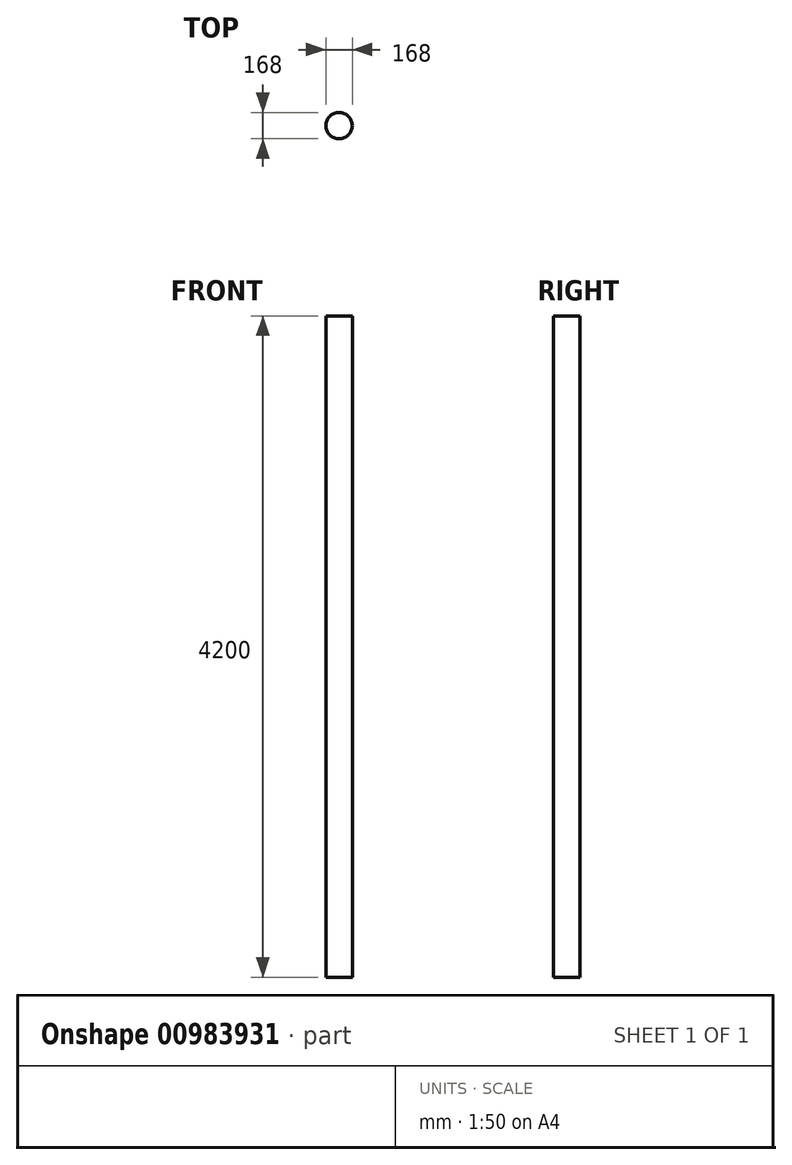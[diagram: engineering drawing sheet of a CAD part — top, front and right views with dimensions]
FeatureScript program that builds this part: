
annotation { "Feature Type Name" : "Feature", "Feature Type Description" : "" }
export const myFeature = defineFeature(function(context is Context, id is Id, definition is map)
    precondition{}
    {
        {
            var Q0;
            Q0=qCreatedBy(makeId("Top.planeOp"),FACE);
            var sketch = newSketch(context, id + "F0", { "sketchPlane" : qUnion([Q0])});
            skCircle(sketch, "E0", {"center": v(0, 0) * mm, "radius": 84 * mm});
            skSolve(sketch);
        }
        {
            var Q0;
            Q0=makeQuery(id+"F0.imprint","IMPRINT",FACE,{"disambiguationData":[TD([[makeQuery(id+"F0.imprint","IMPRINT",EDGE,{"derivedFrom":sQuery(id+"F0.wireOp",EDGE,"E0")}),1.0]])]});
            extrude(context, id + "F1", {"entities" : qUnion([Q0]), "depth" : 4200 * mm, "offsetDistance" : 25 * mm});
        }
    });
